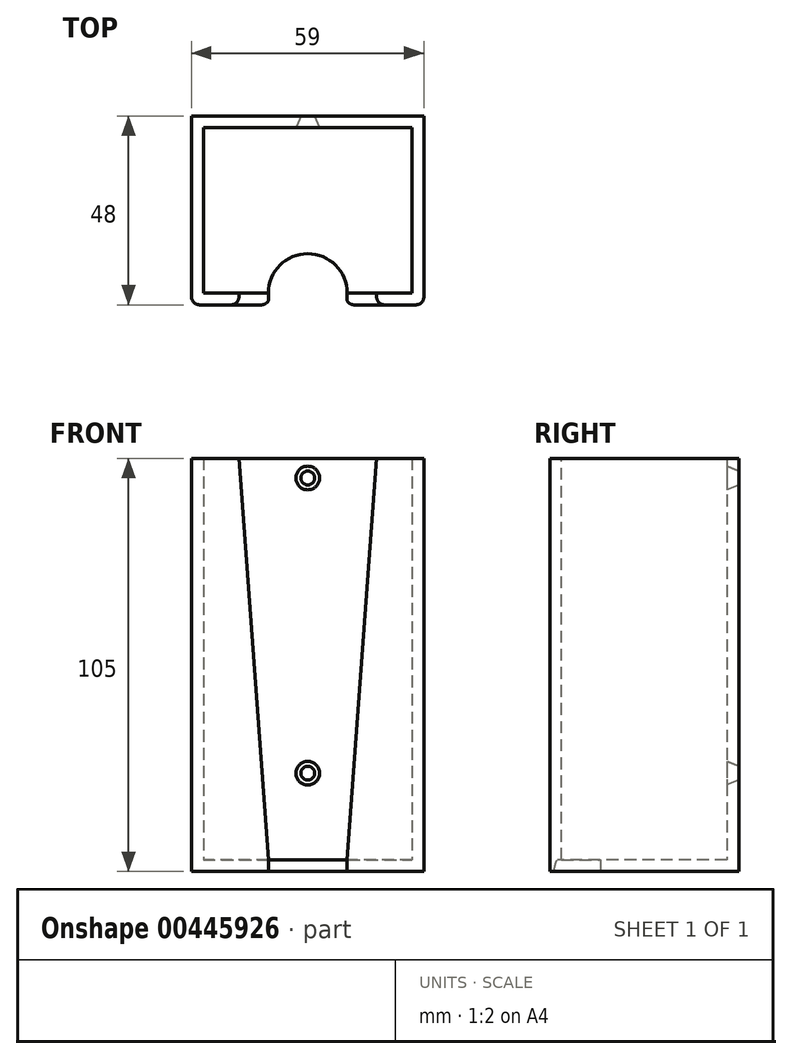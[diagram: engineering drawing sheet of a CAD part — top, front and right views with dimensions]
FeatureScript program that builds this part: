
annotation { "Feature Type Name" : "Feature", "Feature Type Description" : "" }
export const myFeature = defineFeature(function(context is Context, id is Id, definition is map)
    precondition{}
    {
        {
            var Q0;
            Q0=qCreatedBy(makeId("Top.planeOp"),FACE);
            var sketch = newSketch(context, id + "F0", { "sketchPlane" : qUnion([Q0])});
            skLineSegment(sketch, "E0.bottom", {"start": v(-29.5, 24.5) * mm, "end": v(29.5, 24.5) * mm});
            skLineSegment(sketch, "E0.top", {"start": v(-29.5, -23.5) * mm, "end": v(29.5, -23.5) * mm});
            skLineSegment(sketch, "E0.left", {"start": v(-29.5, 24.5) * mm, "end": v(-29.5, -23.5) * mm});
            skLineSegment(sketch, "E0.right", {"start": v(29.5, 24.5) * mm, "end": v(29.5, -23.5) * mm});
            skSolve(sketch);
        }
        {
            var Q0;
            Q0 = qSketchRegion(id + "F0", true);
            extrude(context, id + "F1", {"entities" : qUnion([Q0]), "depth" : 3 * mm});
        }
        {
            var Q0;
            Q0=makeQuery(id+"F1.opExtrude","CAP_FACE",FACE,{"disambiguationData":[OSD([sQuery(id+"F0.wireOp",EDGE,"E0.bottom"),sQuery(id+"F0.wireOp",EDGE,"E0.top"),sQuery(id+"F0.wireOp",EDGE,"E0.left"),sQuery(id+"F0.wireOp",EDGE,"E0.right")])],"isStart":false});
            var sketch = newSketch(context, id + "F2", { "sketchPlane" : qUnion([Q0])});
            skLineSegment(sketch, "E1", {"start": v(-10, -23.5) * mm, "end": v(-29.5, -23.5) * mm});
            skLineSegment(sketch, "E2", {"start": v(-29.5, -23.5) * mm, "end": v(-29.5, 24.5) * mm});
            skLineSegment(sketch, "E3", {"start": v(-29.5, 24.5) * mm, "end": v(29.5, 24.5) * mm});
            skLineSegment(sketch, "E4", {"start": v(29.5, 24.5) * mm, "end": v(29.5, -23.5) * mm});
            skLineSegment(sketch, "E5", {"start": v(29.5, -23.5) * mm, "end": v(10, -23.5) * mm});
            skLineSegment(sketch, "E6", {"start": v(-10, -20.5) * mm, "end": v(-26.5, -20.5) * mm});
            skLineSegment(sketch, "E7", {"start": v(-26.5, -20.5) * mm, "end": v(-26.5, 21.5) * mm});
            skLineSegment(sketch, "E8", {"start": v(-26.5, 21.5) * mm, "end": v(26.5, 21.5) * mm});
            skLineSegment(sketch, "E9", {"start": v(26.5, 21.5) * mm, "end": v(26.5, -20.5) * mm});
            skLineSegment(sketch, "E10", {"start": v(26.5, -20.5) * mm, "end": v(10, -20.5) * mm});
            skLineSegment(sketch, "E11", {"start": v(-10, -20.5) * mm, "end": v(-10, -23.5) * mm});
            skLineSegment(sketch, "E12", {"start": v(10, -20.5) * mm, "end": v(10, -23.5) * mm});
            skSolve(sketch);
        }
        {
            var Q0;
            Q0 = qSketchRegion(id + "F2", true);
            extrude(context, id + "F3", {"entities" : qUnion([Q0]), "operationType" : NewBodyOperationType.ADD, "depth" : 102 * mm});
        }
        {
            var Q0;
            Q0=makeQuery(id+"F3.opExtrude","CAP_EDGE",EDGE,{"disambiguationData":[OSD([sQuery(id+"F2.wireOp",EDGE,"E12")])],"isStart":false});
            var Q1;
            Q1=makeQuery(id+"F3.opExtrude","CAP_EDGE",EDGE,{"disambiguationData":[OSD([sQuery(id+"F2.wireOp",EDGE,"E11")])],"isStart":false});
            chamfer(context, id + "F4", {"entities" : qUnion([Q0, Q1]), "chamferType" : ChamferType.TWO_OFFSETS, "width1" : 7.5 * mm, "oppositeDirection" : false, "width2" : 102 * mm, "tangentPropagation" : true});
        }
        {
            var Q0;
            Q0=makeQuery(id+"F1.opExtrude","CAP_FACE",FACE,{"disambiguationData":[OSD([sQuery(id+"F0.wireOp",EDGE,"E0.bottom"),sQuery(id+"F0.wireOp",EDGE,"E0.top"),sQuery(id+"F0.wireOp",EDGE,"E0.left"),sQuery(id+"F0.wireOp",EDGE,"E0.right")])],"isStart":false});
            var sketch = newSketch(context, id + "F5", { "sketchPlane" : qUnion([Q0])});
            skLineSegment(sketch, "E13", {"start": v(-10, -23.5) * mm, "end": v(-10, -20.5) * mm});
            skLineSegment(sketch, "E14", {"start": v(10, -23.5) * mm, "end": v(10, -20.5) * mm});
            skArc(sketch, "E15", {"start": v(10, -20.5) * mm, "mid": v(0, -10.5) * mm, "end": v(-10, -20.5) * mm});
            skLineSegment(sketch, "E16", {"start": v(-10, -23.5) * mm, "end": v(10, -23.5) * mm});
            skSolve(sketch);
        }
        {
            var Q0;
            Q0 = qSketchRegion(id + "F5", true);
            extrude(context, id + "F6", {"entities" : qUnion([Q0]), "operationType" : NewBodyOperationType.REMOVE, "oppositeDirection" : true, "depth" : 3 * mm});
        }
        {
            var Q0;
            Q0=makeQuery(id+"F3.opExtrude","SWEPT_FACE",FACE,{"disambiguationData":[OSD([sQuery(id+"F2.wireOp",EDGE,"E8")])]});
            var sketch = newSketch(context, id + "F7", { "sketchPlane" : qUnion([Q0])});
            skPoint(sketch, "E17", {"position": v(0, 100) * mm});
            skPoint(sketch, "E18", {"position": v(0, 25) * mm});
            skSolve(sketch);
        }
        {
            var Q0;
            Q0=sQuery(id+"F7.wireOp",VERTEX,"E17");
            var Q1;
            Q1=sQuery(id+"F7.wireOp",VERTEX,"E18");
            var Q2;
            Q2=makeQuery(id+"F1.opExtrude","SWEPT_BODY",BODY,{"disambiguationData":[OSD([sQuery(id+"F0.wireOp",EDGE,"E0.bottom"),sQuery(id+"F0.wireOp",EDGE,"E0.top"),sQuery(id+"F0.wireOp",EDGE,"E0.left"),sQuery(id+"F0.wireOp",EDGE,"E0.right")])]});
            hole(context, id + "F8", {"style" : HoleStyle.C_SINK, "endStyle" : HoleEndStyle.THROUGH, "holeDiameter" : 3.5 * mm, "cSinkDiameter" : 6 * mm, "cSinkAngle" : 45 * degree, "isTappedThrough" : true, "tappedDepth" : 12 * mm, "tapClearance" : 3, "locations" : qUnion([Q0, Q1]), "scope" : qUnion([Q2]), "startStyle" : HoleStartStyle.SKETCH});
        }
        {
            var Q0;
            Q0=makeQuery(id+"F3.boolean.opBoolean","MERGE",EDGE,{"derivedFrom":[makeQuery(id+"F1.opExtrude","SWEPT_EDGE",EDGE,{"disambiguationData":[OSD([sQuery(id+"F0.wireOp",EDGE,"E0.top"),sQuery(id+"F0.wireOp",EDGE,"E0.right")])]}),makeQuery(id+"F3.opExtrude","SWEPT_EDGE",EDGE,{"disambiguationData":[OSD([sQuery(id+"F2.wireOp",EDGE,"E4"),sQuery(id+"F2.wireOp",EDGE,"E5")])]})]});
            var Q1;
            Q1=makeQuery(id+"F3.boolean.opBoolean","MERGE",EDGE,{"derivedFrom":[makeQuery(id+"F1.opExtrude","SWEPT_EDGE",EDGE,{"disambiguationData":[OSD([sQuery(id+"F0.wireOp",EDGE,"E0.top"),sQuery(id+"F0.wireOp",EDGE,"E0.left")])]}),makeQuery(id+"F3.opExtrude","SWEPT_EDGE",EDGE,{"disambiguationData":[OSD([sQuery(id+"F2.wireOp",EDGE,"E1"),sQuery(id+"F2.wireOp",EDGE,"E2")])]})]});
            var Q2;
            Q2=makeQuery(id+"F4.opChamfer","BLEND_EDGE",EDGE,{"blendedFrom":[makeQuery(id+"F3.opExtrude","CAP_EDGE",EDGE,{"disambiguationData":[OSD([sQuery(id+"F2.wireOp",EDGE,"E11")])],"isStart":false}),makeQuery(id+"F3.boolean.opBoolean","MERGE",FACE,{"derivedFrom":[makeQuery(id+"F1.opExtrude","SWEPT_FACE",FACE,{"disambiguationData":[OSD([sQuery(id+"F0.wireOp",EDGE,"E0.top")])]}),makeQuery(id+"F3.opExtrude","SWEPT_FACE",FACE,{"disambiguationData":[OSD([sQuery(id+"F2.wireOp",EDGE,"E1")])]}),makeQuery(id+"F3.opExtrude","SWEPT_FACE",FACE,{"disambiguationData":[OSD([sQuery(id+"F2.wireOp",EDGE,"E5")])]})]})],"blendedInto":[makeQuery(id+"F3.boolean.opBoolean","MERGE",FACE,{"derivedFrom":[makeQuery(id+"F1.opExtrude","SWEPT_FACE",FACE,{"disambiguationData":[OSD([sQuery(id+"F0.wireOp",EDGE,"E0.top")])]}),makeQuery(id+"F3.opExtrude","SWEPT_FACE",FACE,{"disambiguationData":[OSD([sQuery(id+"F2.wireOp",EDGE,"E1")])]}),makeQuery(id+"F3.opExtrude","SWEPT_FACE",FACE,{"disambiguationData":[OSD([sQuery(id+"F2.wireOp",EDGE,"E5")])]})]})]});
            var Q3;
            Q3=makeQuery(id+"F6.boolean.opBoolean","COPY",EDGE,{"derivedFrom":makeQuery(id+"F6.opExtrude","SWEPT_EDGE",EDGE,{"disambiguationData":[OSD([sQuery(id+"F5.wireOp",EDGE,"E13"),sQuery(id+"F5.wireOp",EDGE,"E16")])]})});
            var Q4;
            Q4=makeQuery(id+"F6.boolean.opBoolean","COPY",EDGE,{"derivedFrom":makeQuery(id+"F6.opExtrude","SWEPT_EDGE",EDGE,{"disambiguationData":[OSD([sQuery(id+"F5.wireOp",EDGE,"E14"),sQuery(id+"F5.wireOp",EDGE,"E16")])]})});
            var Q5;
            Q5=makeQuery(id+"F4.opChamfer","BLEND_EDGE",EDGE,{"blendedFrom":[makeQuery(id+"F3.opExtrude","CAP_EDGE",EDGE,{"disambiguationData":[OSD([sQuery(id+"F2.wireOp",EDGE,"E12")])],"isStart":false}),makeQuery(id+"F3.boolean.opBoolean","MERGE",FACE,{"derivedFrom":[makeQuery(id+"F1.opExtrude","SWEPT_FACE",FACE,{"disambiguationData":[OSD([sQuery(id+"F0.wireOp",EDGE,"E0.top")])]}),makeQuery(id+"F3.opExtrude","SWEPT_FACE",FACE,{"disambiguationData":[OSD([sQuery(id+"F2.wireOp",EDGE,"E1")])]}),makeQuery(id+"F3.opExtrude","SWEPT_FACE",FACE,{"disambiguationData":[OSD([sQuery(id+"F2.wireOp",EDGE,"E5")])]})]})],"blendedInto":[makeQuery(id+"F3.boolean.opBoolean","MERGE",FACE,{"derivedFrom":[makeQuery(id+"F1.opExtrude","SWEPT_FACE",FACE,{"disambiguationData":[OSD([sQuery(id+"F0.wireOp",EDGE,"E0.top")])]}),makeQuery(id+"F3.opExtrude","SWEPT_FACE",FACE,{"disambiguationData":[OSD([sQuery(id+"F2.wireOp",EDGE,"E1")])]}),makeQuery(id+"F3.opExtrude","SWEPT_FACE",FACE,{"disambiguationData":[OSD([sQuery(id+"F2.wireOp",EDGE,"E5")])]})]})]});
            fillet(context, id + "F9", {"entities" : qUnion([Q0, Q1, Q2, Q3, Q4, Q5]), "radius" : 2 * mm, "tangentPropagation" : true, "allowEdgeOverflow" : false});
        }
    });
